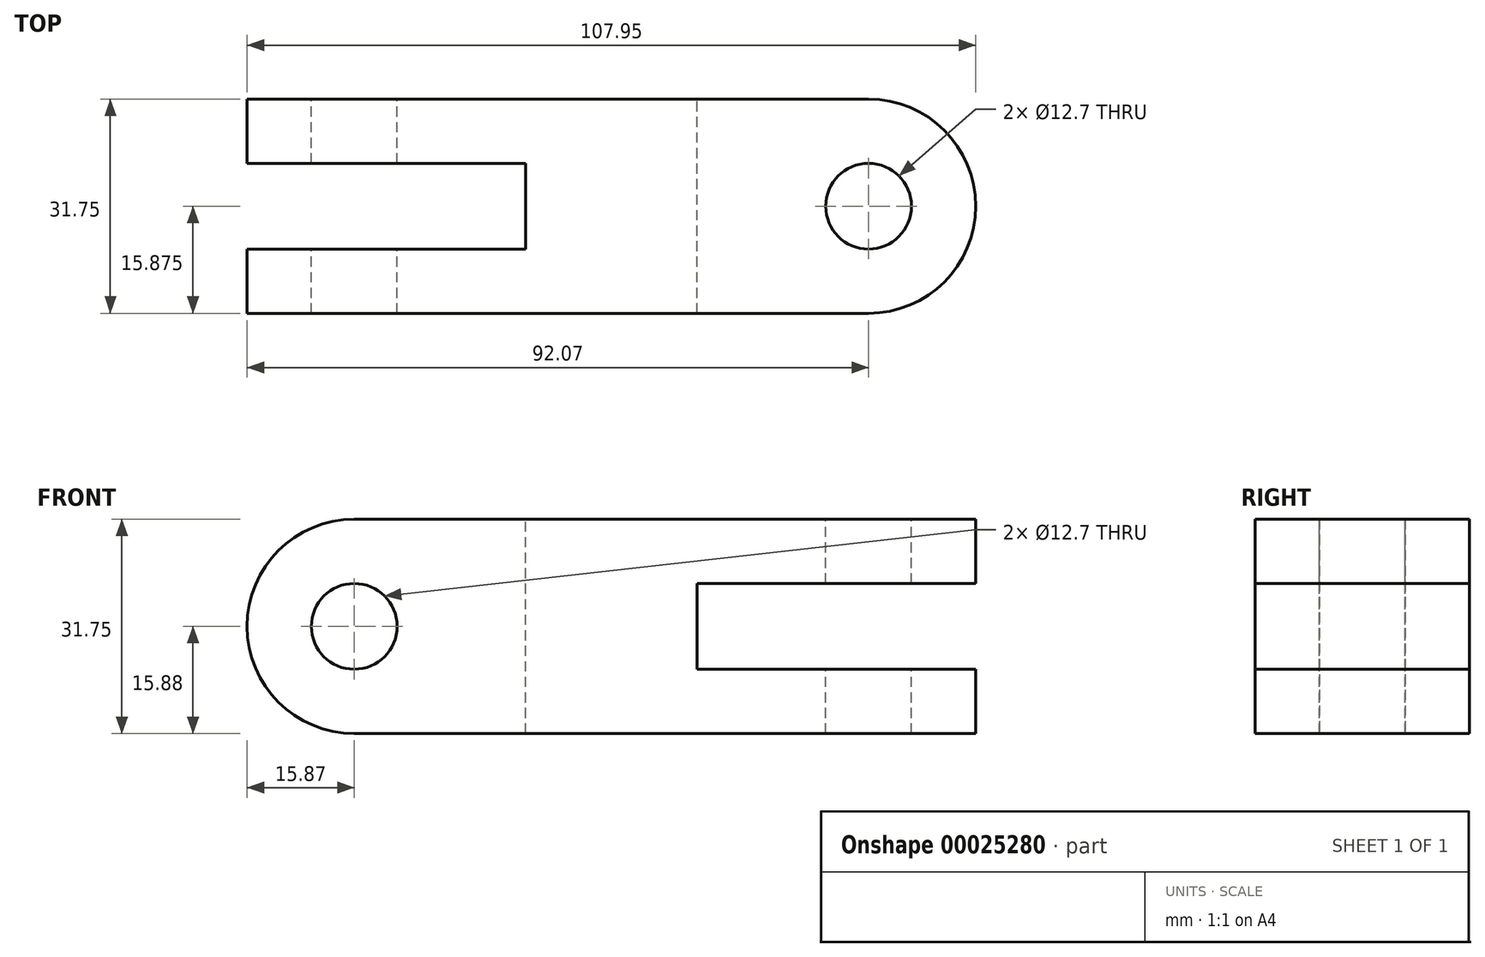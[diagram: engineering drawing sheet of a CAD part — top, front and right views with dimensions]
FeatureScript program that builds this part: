
annotation { "Feature Type Name" : "Feature", "Feature Type Description" : "" }
export const myFeature = defineFeature(function(context is Context, id is Id, definition is map)
    precondition{}
    {
        {
            var Q0;
            Q0=qCreatedBy(makeId("Front.planeOp"),FACE);
            var sketch = newSketch(context, id + "F0", { "sketchPlane" : qUnion([Q0])});
            skLineSegment(sketch, "E0.bottom", {"start": v(-51.5, 13.25) * mm, "end": v(56.45, 13.25) * mm});
            skLineSegment(sketch, "E0.top", {"start": v(-51.5, -18.5) * mm, "end": v(56.45, -18.5) * mm});
            skLineSegment(sketch, "E0.left", {"start": v(-51.5, 13.25) * mm, "end": v(-51.5, -18.5) * mm});
            skLineSegment(sketch, "E0.right", {"start": v(56.45, 13.25) * mm, "end": v(56.45, -18.5) * mm});
            skLineSegment(sketch, "E1.0", {"start": v(-35.63, 3.73) * mm, "end": v(-35.63, -8.97) * mm, "construction": true});
            skArc(sketch, "E2", {"start": v(-35.63, 13.25) * mm, "mid": v(-51.5, -2.62) * mm, "end": v(-35.63, -18.5) * mm});
            skCircle(sketch, "E3", {"center": v(-35.63, -2.62) * mm, "radius": 6.35 * mm});
            skLineSegment(sketch, "E4.0", {"start": v(15.17, 3.73) * mm, "end": v(15.17, -8.97) * mm});
            skLineSegment(sketch, "E5.trimOffspring", {"start": v(15.17, -8.97) * mm, "end": v(56.45, -8.97) * mm});
            skLineSegment(sketch, "E6.trimOffspring", {"start": v(15.17, 3.73) * mm, "end": v(56.45, 3.73) * mm});
            skSolve(sketch);
        }
        {
            var Q0;
            Q0=makeQuery(id+"F0.imprint","IMPRINT",FACE,{"disambiguationData":[TD([[makeQuery(id+"F0.imprint","IMPRINT",EDGE,{"derivedFrom":sQuery(id+"F0.wireOp",EDGE,"E3")}),-1.0]])]});
            extrude(context, id + "F1", {"entities" : qUnion([Q0]), "depth" : 31.75 * mm});
        }
        {
            var Q0;
            Q0=makeQuery(id+"F1.opExtrude","SWEPT_FACE",FACE,{"disambiguationData":[OSD([sQuery(id+"F0.wireOp",EDGE,"E0.bottom")])]});
            var sketch = newSketch(context, id + "F2", { "sketchPlane" : qUnion([Q0])});
            skLineSegment(sketch, "E7.0", {"start": v(-51.5, -31.75) * mm, "end": v(-51.5, 0) * mm});
            skLineSegment(sketch, "E8", {"start": v(-51.5, 0) * mm, "end": v(56.45, 0) * mm});
            skLineSegment(sketch, "E9", {"start": v(-51.5, -31.75) * mm, "end": v(56.45, -31.75) * mm});
            skLineSegment(sketch, "E10.0", {"start": v(40.57, -31.75) * mm, "end": v(40.57, 0) * mm});
            skCircle(sketch, "E11", {"center": v(40.57, -15.88) * mm, "radius": 15.88 * mm});
            skCircle(sketch, "E12", {"center": v(40.57, -15.88) * mm, "radius": 6.35 * mm});
            skLineSegment(sketch, "E13.0", {"start": v(-51.5, -9.53) * mm, "end": v(56.45, -9.53) * mm});
            skLineSegment(sketch, "E14.0", {"start": v(-51.5, -22.23) * mm, "end": v(56.45, -22.23) * mm});
            skLineSegment(sketch, "E15.0", {"start": v(-10.23, -31.75) * mm, "end": v(-10.23, 0) * mm});
            skSolve(sketch);
        }
        {
            var Q0;
            {var subQ1=sQuery(id+"F2.wireOp",EDGE,"E13.0");var subQ5=sQuery(id+"F2.wireOp",EDGE,"E11");var subQ6=makeQuery(id+"F2.imprint","INTERSECT",VERTEX,{"disambiguationData":[OD(0.0)],"derivedFrom":[subQ5,subQ1]});Q0=makeQuery(id+"F2.imprint","IMPRINT",FACE,{"disambiguationData":[TD([[makeQuery(id+"F2.imprint","IMPRINT",EDGE,{"disambiguationData":[TD([[subQ6,-1.0]])],"derivedFrom":subQ5}),-1.0]])]});}
            var Q1;
            {var subQ0=sQuery(id+"F2.wireOp",EDGE,"E12");var subQ1=sQuery(id+"F2.wireOp",EDGE,"E10.0");var subQ3=makeQuery(id+"F2.imprint","INTERSECT",VERTEX,{"derivedFrom":[subQ1,subQ0,sQuery(id+"F2.wireOp",EDGE,"E14.0")]});Q1=makeQuery(id+"F2.imprint","IMPRINT",FACE,{"disambiguationData":[TD([[makeQuery(id+"F2.imprint","IMPRINT",EDGE,{"disambiguationData":[TD([[subQ3,-1.0]])],"derivedFrom":subQ1}),-1.0]])]});}
            var Q2;
            {var subQ0=sQuery(id+"F2.wireOp",EDGE,"E12");var subQ1=sQuery(id+"F2.wireOp",EDGE,"E10.0");var subQ3=makeQuery(id+"F2.imprint","INTERSECT",VERTEX,{"derivedFrom":[subQ1,subQ0,sQuery(id+"F2.wireOp",EDGE,"E14.0")]});Q2=makeQuery(id+"F2.imprint","IMPRINT",FACE,{"disambiguationData":[TD([[makeQuery(id+"F2.imprint","IMPRINT",EDGE,{"disambiguationData":[TD([[subQ3,-1.0]])],"derivedFrom":subQ1}),1.0]])]});}
            var Q3;
            {var subQ1=sQuery(id+"F2.wireOp",EDGE,"E14.0");var subQ5=sQuery(id+"F2.wireOp",EDGE,"E11");var subQ6=makeQuery(id+"F2.imprint","INTERSECT",VERTEX,{"disambiguationData":[OD(1.0)],"derivedFrom":[subQ5,subQ1]});Q3=makeQuery(id+"F2.imprint","IMPRINT",FACE,{"disambiguationData":[TD([[makeQuery(id+"F2.imprint","IMPRINT",EDGE,{"disambiguationData":[TD([[subQ6,1.0]])],"derivedFrom":subQ5}),-1.0]])]});}
            var Q4;
            {var subQ1=sQuery(id+"F2.wireOp",EDGE,"E11");var subQ3=sQuery(id+"F2.wireOp",EDGE,"E14.0");var subQ5=makeQuery(id+"F2.imprint","INTERSECT",VERTEX,{"disambiguationData":[OD(1.0)],"derivedFrom":[subQ1,subQ3]});Q4=makeQuery(id+"F2.imprint","IMPRINT",FACE,{"disambiguationData":[TD([[makeQuery(id+"F2.imprint","IMPRINT",EDGE,{"disambiguationData":[TD([[subQ5,-1.0]])],"derivedFrom":subQ1}),-1.0]])]});}
            var Q5;
            {var subQ1=sQuery(id+"F2.wireOp",EDGE,"E11");var subQ3=sQuery(id+"F2.wireOp",EDGE,"E13.0");var subQ5=makeQuery(id+"F2.imprint","INTERSECT",VERTEX,{"disambiguationData":[OD(0.0)],"derivedFrom":[subQ1,subQ3]});Q5=makeQuery(id+"F2.imprint","IMPRINT",FACE,{"disambiguationData":[TD([[makeQuery(id+"F2.imprint","IMPRINT",EDGE,{"disambiguationData":[TD([[subQ5,1.0]])],"derivedFrom":subQ1}),-1.0]])]});}
            var Q6;
            {var subQ3=sQuery(id+"F2.wireOp",EDGE,"E13.0");var subQ5=sQuery(id+"F2.wireOp",EDGE,"E15.0");var subQ7=makeQuery(id+"F2.imprint","INTERSECT",VERTEX,{"derivedFrom":[subQ3,subQ5]});Q6=makeQuery(id+"F2.imprint","IMPRINT",FACE,{"disambiguationData":[TD([[makeQuery(id+"F2.imprint","IMPRINT",EDGE,{"disambiguationData":[TD([[subQ7,1.0]])],"derivedFrom":subQ5}),1.0]])]});}
            var Q7;
            {var subQ3=sQuery(id+"F2.wireOp",EDGE,"E13.0");var subQ5=sQuery(id+"F2.wireOp",EDGE,"E7.0");var subQ7=makeQuery(id+"F2.imprint","INTERSECT",VERTEX,{"derivedFrom":[subQ5,subQ3]});Q7=makeQuery(id+"F2.imprint","IMPRINT",FACE,{"disambiguationData":[TD([[makeQuery(id+"F2.imprint","IMPRINT",EDGE,{"disambiguationData":[TD([[subQ7,1.0]])],"derivedFrom":subQ5}),-1.0]])]});}
            extrude(context, id + "F3", {"entities" : qUnion([Q0, Q1, Q2, Q3, Q4, Q5, Q6, Q7]), "operationType" : NewBodyOperationType.REMOVE, "endBound" : BoundingType.THROUGH_ALL, "oppositeDirection" : true, "depth" : 25.4 * mm});
        }
    });
